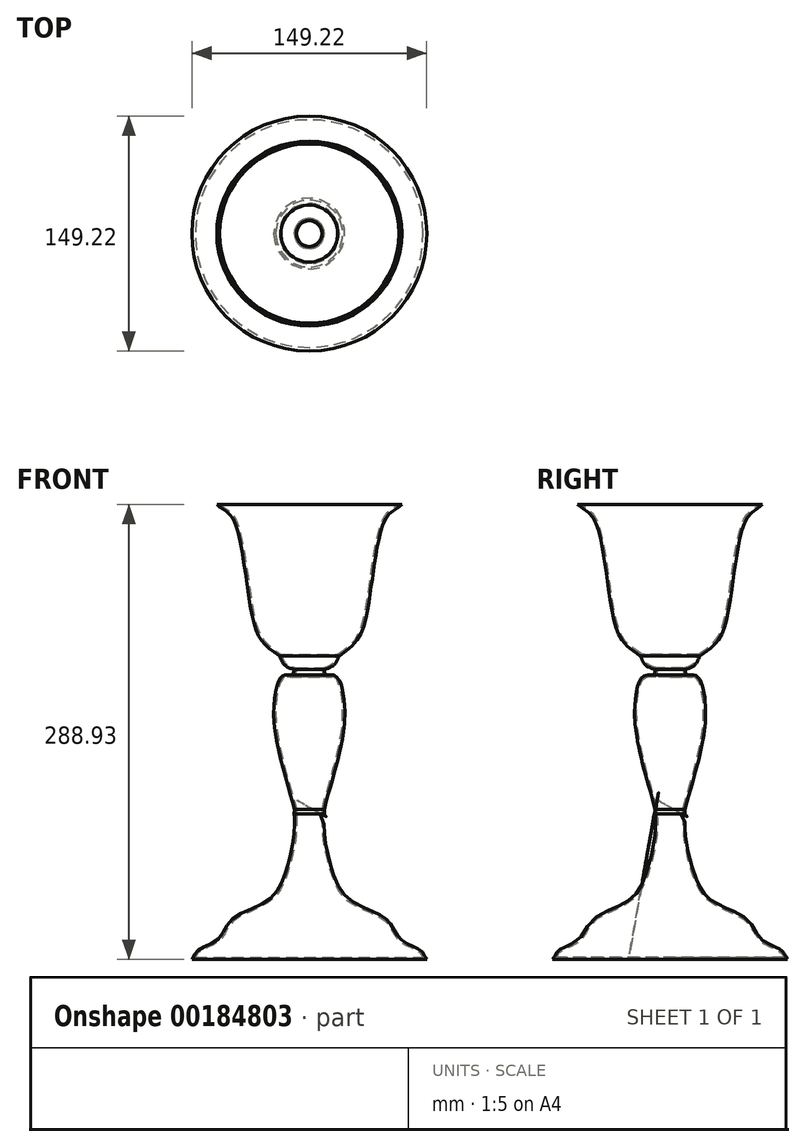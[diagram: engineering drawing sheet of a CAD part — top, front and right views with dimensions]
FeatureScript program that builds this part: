
annotation { "Feature Type Name" : "Feature", "Feature Type Description" : "" }
export const myFeature = defineFeature(function(context is Context, id is Id, definition is map)
    precondition{}
    {
        {
            var Q0;
            Q0=qCreatedBy(makeId("Front.planeOp"),FACE);
            var sketch = newSketch(context, id + "F0", { "sketchPlane" : qUnion([Q0])});
            skLineSegment(sketch, "E0", {"start": v(0, 0) * mm, "end": v(0, 288.93) * mm});
            skLineSegment(sketch, "E1", {"start": v(0, 288.93) * mm, "end": v(58.74, 288.93) * mm});
            skLineSegment(sketch, "E2", {"start": v(0, 0) * mm, "end": v(74.61, 0) * mm});
            skFitSpline(sketch, "E3", {"points": [v(58.74, 288.93) * mm, v(48.7, 280.3) * mm, v(34.93, 212.75) * mm, v(19.05, 192.89) * mm], "startDerivative": vector(-38.8, -45.73) * mm, "endDerivative": vector(-85.9, -59.21) * mm});
            skFitSpline(sketch, "E4", {"points": [v(19.05, 192.89) * mm, v(9.52, 184.15) * mm], "startDerivative": vector(-5.34, -10.28) * mm, "endDerivative": vector(-23.23, -5.56) * mm});
            skFitSpline(sketch, "E5", {"points": [v(9.52, 184.15) * mm, v(13.67, 180.66) * mm, v(18.33, 178.59) * mm, v(22.23, 149.6) * mm, v(9.52, 95.25) * mm], "startDerivative": vector(0.44, -92.6) * mm, "endDerivative": vector(-25.35, -104) * mm});
            skFitSpline(sketch, "E6", {"points": [v(9.52, 95.25) * mm, v(9.53, 92.37) * mm, v(9.66, 80) * mm, v(14.83, 55.94) * mm, v(25.48, 38.1) * mm, v(49.28, 25.18) * mm, v(58, 12.85) * mm, v(70.72, 5.77) * mm, v(74.61, 0) * mm, v(94.96, -25.97) * mm], "startDerivative": vector(0, -236.84) * mm, "endDerivative": vector(22.53, -131.1) * mm});
            skSolve(sketch);
        }
        {
            var Q0;
            Q0=makeQuery(id+"F0.imprint","IMPRINT",FACE,{"disambiguationData":[TD([[makeQuery(id+"F0.imprint","IMPRINT",EDGE,{"derivedFrom":sQuery(id+"F0.wireOp",EDGE,"E0")}),-1.0]])]});
            var Q1;
            Q1=sQuery(id+"F0.wireOp",EDGE,"E0");
            revolve(context, id + "F1", {"entities" : qUnion([Q0]), "axis" : qUnion([Q1]), "revolveType" : RevolveType.FULL});
        }
        {
            var Q0;
            Q0=makeQuery(id+"F1.opRevolve","SWEPT_FACE",FACE,{"disambiguationData":[OSD([sQuery(id+"F0.wireOp",EDGE,"E1")])]});
            shell(context, id + "F2", {"entities" : qUnion([Q0]), "thickness" : 1.27 * mm});
        }
    });
